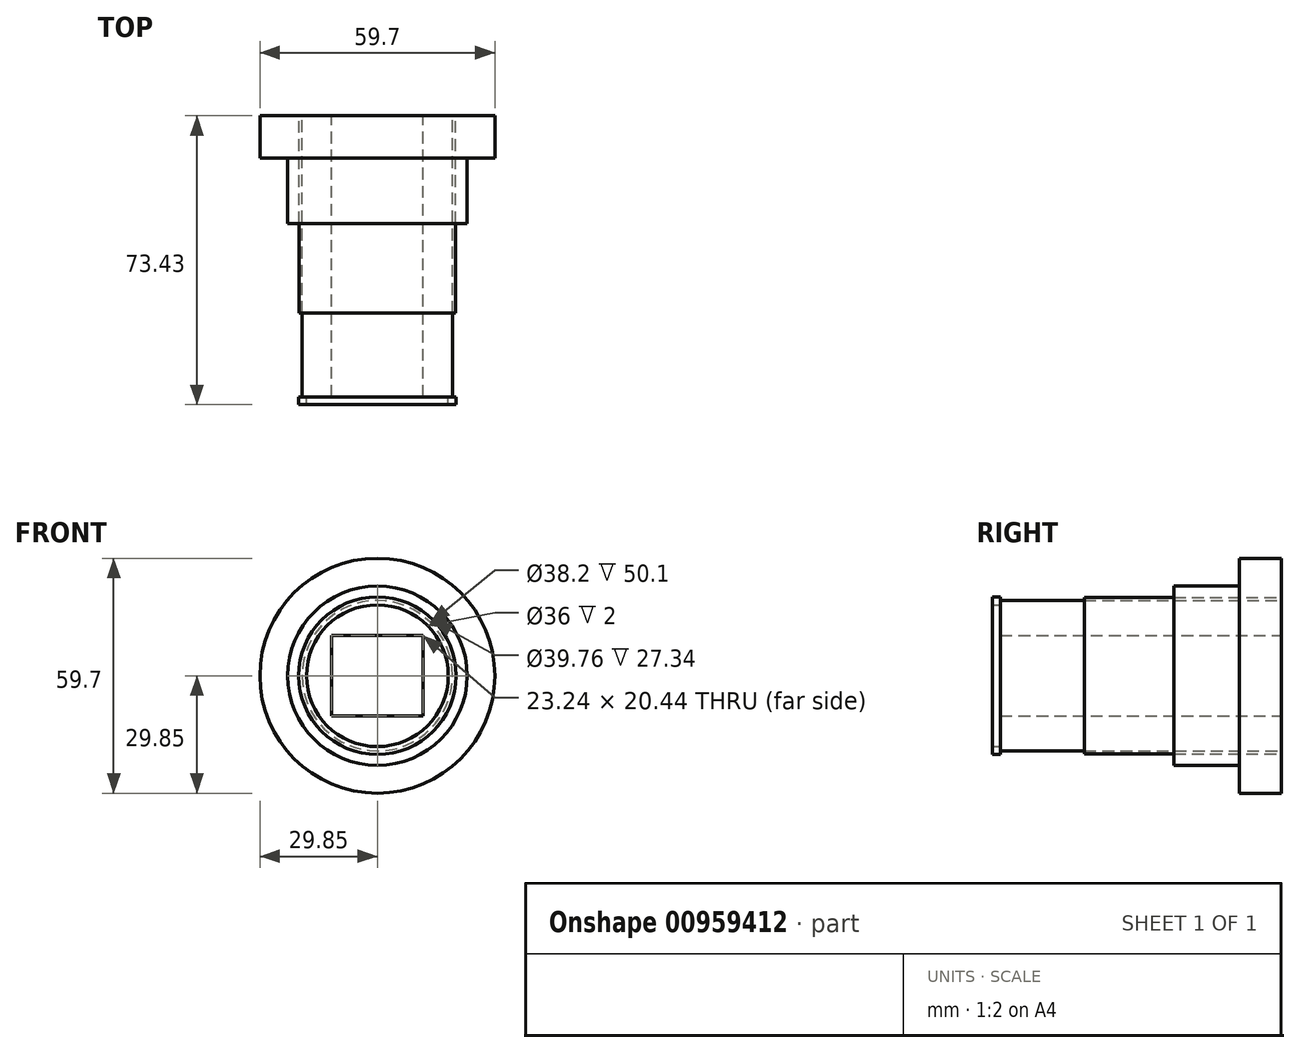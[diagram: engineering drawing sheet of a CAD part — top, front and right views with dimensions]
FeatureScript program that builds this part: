
annotation { "Feature Type Name" : "Feature", "Feature Type Description" : "" }
export const myFeature = defineFeature(function(context is Context, id is Id, definition is map)
    precondition{}
    {
        {
            var Q0;
            Q0=qCreatedBy(makeId("Front.planeOp"),FACE);
            var sketch = newSketch(context, id + "F0", { "sketchPlane" : qUnion([Q0])});
            skCircle(sketch, "E0", {"center": v(0, 0) * mm, "radius": 19.1 * mm});
            skCircle(sketch, "E1", {"center": v(0, 0) * mm, "radius": 19.88 * mm});
            skCircle(sketch, "E2", {"center": v(0, 0) * mm, "radius": 22.8 * mm});
            skCircle(sketch, "E3", {"center": v(0, 0) * mm, "radius": 29.85 * mm});
            skSolve(sketch);
        }
        {
            var Q0;
            Q0=qCreatedBy(makeId("Front.planeOp"),FACE);
            var sketch = newSketch(context, id + "F1", { "sketchPlane" : qUnion([Q0])});
            skLineSegment(sketch, "E4.bottom", {"start": v(-11.62, 10.22) * mm, "end": v(11.62, 10.22) * mm});
            skLineSegment(sketch, "E4.top", {"start": v(-11.62, -10.22) * mm, "end": v(11.62, -10.22) * mm});
            skLineSegment(sketch, "E4.left", {"start": v(-11.62, 10.22) * mm, "end": v(-11.62, -10.22) * mm});
            skLineSegment(sketch, "E4.right", {"start": v(11.62, 10.22) * mm, "end": v(11.62, -10.22) * mm});
            skLineSegment(sketch, "E5", {"start": v(0, 0) * mm, "end": v(11.62, 0) * mm, "construction": true});
            skLineSegment(sketch, "E6", {"start": v(0, 0) * mm, "end": v(0, 10.22) * mm, "construction": true});
            skSolve(sketch);
        }
        {
            var Q0;
            Q0=makeQuery(id+"F0.imprint","IMPRINT",FACE,{"disambiguationData":[TD([[makeQuery(id+"F0.imprint","IMPRINT",EDGE,{"derivedFrom":sQuery(id+"F0.wireOp",EDGE,"E2")}),-1.0]])]});
            extrude(context, id + "F2", {"entities" : qUnion([Q0]), "depth" : 10.7 * mm, "offsetDistance" : 25 * mm});
        }
        {
            var Q0;
            Q0=makeQuery(id+"F0.imprint","IMPRINT",FACE,{"disambiguationData":[TD([[makeQuery(id+"F0.imprint","IMPRINT",EDGE,{"derivedFrom":sQuery(id+"F0.wireOp",EDGE,"E1")}),-1.0]])]});
            extrude(context, id + "F3", {"entities" : qUnion([Q0]), "operationType" : NewBodyOperationType.ADD, "depth" : 27.34 * mm, "offsetDistance" : 25 * mm});
        }
        {
            var Q0;
            Q0=makeQuery(id+"F0.imprint","IMPRINT",FACE,{"disambiguationData":[TD([[makeQuery(id+"F0.imprint","IMPRINT",EDGE,{"derivedFrom":sQuery(id+"F0.wireOp",EDGE,"E0")}),-1.0]])]});
            extrude(context, id + "F4", {"entities" : qUnion([Q0]), "depth" : 50.1 * mm, "offsetDistance" : 25 * mm});
        }
        {
            var Q0;
            Q0=makeQuery(id+"F0.imprint","IMPRINT",FACE,{"disambiguationData":[TD([[makeQuery(id+"F0.imprint","IMPRINT",EDGE,{"derivedFrom":sQuery(id+"F0.wireOp",EDGE,"E0")}),1.0]])]});
            extrude(context, id + "F5", {"entities" : qUnion([Q0]), "depth" : 71.43 * mm, "offsetDistance" : 25 * mm});
        }
        {
            var Q0;
            Q0=makeQuery(id+"F1.imprint","IMPRINT",FACE,{"disambiguationData":[TD([[makeQuery(id+"F1.imprint","IMPRINT",EDGE,{"derivedFrom":sQuery(id+"F1.wireOp",EDGE,"E4.bottom")}),-1.0]])]});
            extrude(context, id + "F6", {"entities" : qUnion([Q0]), "operationType" : NewBodyOperationType.REMOVE, "depth" : 72 * mm, "offsetDistance" : 25 * mm});
        }
        {
            var Q0;
            Q0=makeQuery(id+"F5.opExtrude","CAP_FACE",FACE,{"disambiguationData":[OSD([sQuery(id+"F0.wireOp",EDGE,"E0")])],"isStart":false});
            var sketch = newSketch(context, id + "F7", { "sketchPlane" : qUnion([Q0])});
            skCircle(sketch, "E7", {"center": v(0, 0) * mm, "radius": 18 * mm});
            skCircle(sketch, "E8", {"center": v(0, 0) * mm, "radius": 20 * mm});
            skSolve(sketch);
        }
        {
            var Q0;
            Q0=makeQuery(id+"F7.imprint","IMPRINT",FACE,{"disambiguationData":[TD([[makeQuery(id+"F7.imprint","IMPRINT",EDGE,{"derivedFrom":sQuery(id+"F7.wireOp",EDGE,"E8")}),1.0]])]});
            var Q1;
            Q1=makeQuery(id+"F7.imprint","IMPRINT",FACE,{"disambiguationData":[TD([[makeQuery(id+"F7.imprint","IMPRINT",EDGE,{"derivedFrom":sQuery(id+"F7.wireOp",EDGE,"E7")}),-1.0]])]});
            extrude(context, id + "F8", {"entities" : qUnion([Q0, Q1]), "operationType" : NewBodyOperationType.ADD, "depth" : 2 * mm, "offsetDistance" : 25 * mm});
        }
    });
